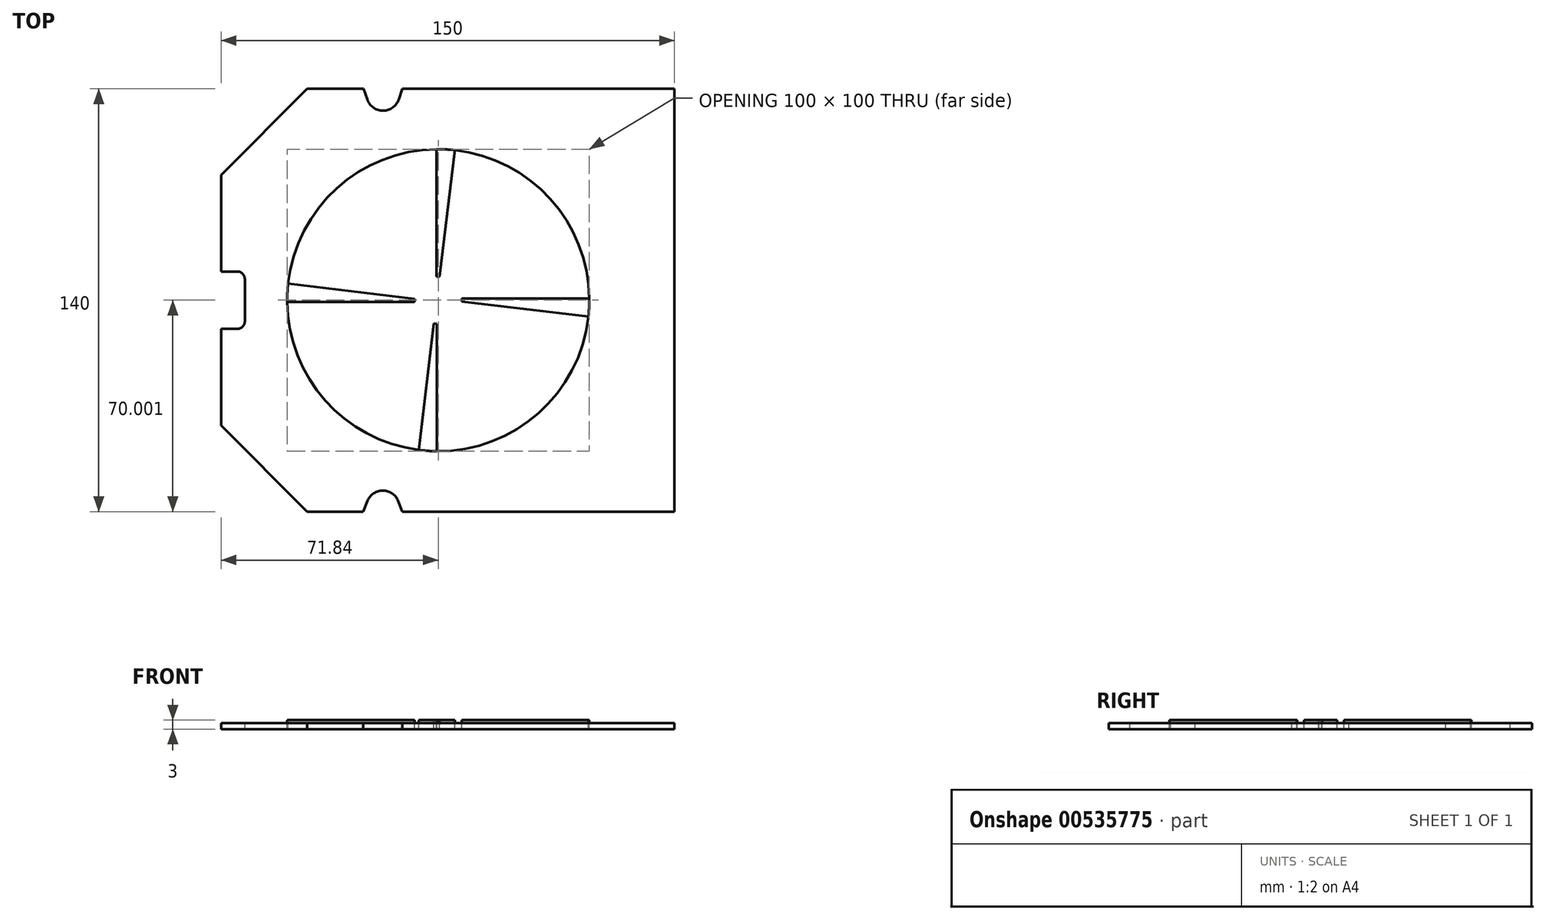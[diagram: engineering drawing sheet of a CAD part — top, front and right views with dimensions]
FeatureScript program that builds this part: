
annotation { "Feature Type Name" : "Feature", "Feature Type Description" : "" }
export const myFeature = defineFeature(function(context is Context, id is Id, definition is map)
    precondition{}
    {
        {
            var Q0;
            Q0=qCreatedBy(makeId("Top.planeOp"),FACE);
            var sketch = newSketch(context, id + "F0", { "sketchPlane" : qUnion([Q0])});
            skLineSegment(sketch, "E0.bottom", {"start": v(75, -70) * mm, "end": v(-75, -70) * mm});
            skLineSegment(sketch, "E0.top", {"start": v(75, 70) * mm, "end": v(-75, 70) * mm});
            skLineSegment(sketch, "E0.left", {"start": v(75, -70) * mm, "end": v(75, 70) * mm});
            skLineSegment(sketch, "E0.right", {"start": v(-75, -70) * mm, "end": v(-75, 70) * mm});
            skPoint(sketch, "E0.middle", {"position": v(0, 0) * mm});
            skSolve(sketch);
        }
        {
            var Q0;
            Q0=qSketchRegion(id+"F0",true);
            extrude(context, id + "F1", {"entities" : qUnion([Q0]), "depth" : 2 * mm, "offsetDistance" : 25 * mm});
        }
        {
            var Q0;
            Q0=makeQuery(id+"F1.opExtrude","CAP_FACE",FACE,{"disambiguationData":[OSD([sQuery(id+"F0.wireOp",EDGE,"E0.bottom"),sQuery(id+"F0.wireOp",EDGE,"E0.top"),sQuery(id+"F0.wireOp",EDGE,"E0.left"),sQuery(id+"F0.wireOp",EDGE,"E0.right")])],"isStart":false});
            var sketch = newSketch(context, id + "F2", { "sketchPlane" : qUnion([Q0])});
            skLineSegment(sketch, "E1", {"start": v(-75, 41.5) * mm, "end": v(-46.5, 70) * mm});
            skLineSegment(sketch, "E2", {"start": v(-75, -41.5) * mm, "end": v(-46.5, -70) * mm});
            skSolve(sketch);
        }
        {
            var Q0;
            Q0=qSketchRegion(id+"F2",true);
            var Q1;
            {var subQ0=sQuery(id+"F2.wireOp",EDGE,"E1");Q1=makeQuery(id+"F2.imprint","IMPRINT",FACE,{"disambiguationData":[TD([[makeQuery(id+"F2.imprint","IMPRINT",EDGE,{"derivedFrom":subQ0}),1.0]])]});}
            var Q2;
            {var subQ0=sQuery(id+"F2.wireOp",EDGE,"E2");Q2=makeQuery(id+"F2.imprint","IMPRINT",FACE,{"disambiguationData":[TD([[makeQuery(id+"F2.imprint","IMPRINT",EDGE,{"derivedFrom":subQ0}),-1.0]])]});}
            extrude(context, id + "F3", {"entities" : qUnion([Q0, Q1, Q2]), "operationType" : NewBodyOperationType.REMOVE, "endBound" : BoundingType.THROUGH_ALL, "oppositeDirection" : true, "depth" : 25 * mm, "offsetDistance" : 25 * mm});
        }
        {
            var Q0;
            Q0=makeQuery(id+"F1.opExtrude","CAP_FACE",FACE,{"disambiguationData":[OSD([sQuery(id+"F0.wireOp",EDGE,"E0.bottom"),sQuery(id+"F0.wireOp",EDGE,"E0.top"),sQuery(id+"F0.wireOp",EDGE,"E0.left"),sQuery(id+"F0.wireOp",EDGE,"E0.right")])],"isStart":false});
            var sketch = newSketch(context, id + "F4", { "sketchPlane" : qUnion([Q0])});
            skLineSegment(sketch, "E3", {"start": v(-75, 9.5) * mm, "end": v(-69.68, 9.5) * mm});
            skLineSegment(sketch, "E4", {"start": v(-67.18, 7) * mm, "end": v(-67.18, -7) * mm});
            skArc(sketch, "E5", {"start": v(-67.18, 7) * mm, "mid": v(-67.91, 8.77) * mm, "end": v(-69.68, 9.5) * mm});
            skLineSegment(sketch, "E6", {"start": v(-75, -9.5) * mm, "end": v(-69.68, -9.5) * mm});
            skArc(sketch, "E7", {"start": v(-69.68, -9.5) * mm, "mid": v(-67.91, -8.77) * mm, "end": v(-67.18, -7) * mm});
            skSolve(sketch);
        }
        {
            var Q0;
            Q0=qSketchRegion(id+"F4",true);
            var Q1;
            {var subQ1=sQuery(id+"F4.wireOp",EDGE,"E3");Q1=makeQuery(id+"F4.imprint","IMPRINT",FACE,{"disambiguationData":[TD([[makeQuery(id+"F4.imprint","IMPRINT",EDGE,{"derivedFrom":subQ1}),-1.0]])]});}
            extrude(context, id + "F5", {"entities" : qUnion([Q0, Q1]), "operationType" : NewBodyOperationType.REMOVE, "endBound" : BoundingType.THROUGH_ALL, "oppositeDirection" : true, "depth" : 25 * mm, "offsetDistance" : 25 * mm});
        }
        {
            var Q0;
            Q0=makeQuery(id+"F1.opExtrude","CAP_FACE",FACE,{"disambiguationData":[OSD([sQuery(id+"F0.wireOp",EDGE,"E0.bottom"),sQuery(id+"F0.wireOp",EDGE,"E0.top"),sQuery(id+"F0.wireOp",EDGE,"E0.left"),sQuery(id+"F0.wireOp",EDGE,"E0.right")])],"isStart":false});
            var sketch = newSketch(context, id + "F6", { "sketchPlane" : qUnion([Q0])});
            skArc(sketch, "E8", {"start": v(-26.63, 66.43) * mm, "mid": v(-21.44, 62.74) * mm, "end": v(-16.24, 66.43) * mm});
            skArc(sketch, "E9", {"start": v(-16.42, -66.5) * mm, "mid": v(-21.52, -63.06) * mm, "end": v(-26.61, -66.5) * mm});
            skLineSegment(sketch, "E10", {"start": v(-27.88, 70) * mm, "end": v(-26.63, 66.43) * mm});
            skLineSegment(sketch, "E11", {"start": v(-15, 70) * mm, "end": v(-16.24, 66.43) * mm});
            skLineSegment(sketch, "E12", {"start": v(-26.61, -66.5) * mm, "end": v(-28.03, -70) * mm});
            skLineSegment(sketch, "E13", {"start": v(-16.42, -66.5) * mm, "end": v(-15, -70) * mm});
            skSolve(sketch);
        }
        {
            var Q0;
            Q0=qSketchRegion(id+"F6",true);
            var Q1;
            Q1=makeQuery(id+"F6.imprint","IMPRINT",FACE,{"disambiguationData":[TD([[makeQuery(id+"F6.imprint","IMPRINT",EDGE,{"derivedFrom":sQuery(id+"F6.wireOp",EDGE,"E9")}),1.0]])]});
            var Q2;
            Q2=makeQuery(id+"F6.imprint","IMPRINT",FACE,{"disambiguationData":[TD([[makeQuery(id+"F6.imprint","IMPRINT",EDGE,{"derivedFrom":sQuery(id+"F6.wireOp",EDGE,"E8")}),1.0]])]});
            extrude(context, id + "F7", {"entities" : qUnion([Q0, Q1, Q2]), "operationType" : NewBodyOperationType.REMOVE, "endBound" : BoundingType.THROUGH_ALL, "oppositeDirection" : true, "depth" : 25 * mm, "offsetDistance" : 25 * mm});
        }
        {
            var Q0;
            Q0=makeQuery(id+"F1.opExtrude","CAP_FACE",FACE,{"disambiguationData":[OSD([sQuery(id+"F0.wireOp",EDGE,"E0.bottom"),sQuery(id+"F0.wireOp",EDGE,"E0.top"),sQuery(id+"F0.wireOp",EDGE,"E0.left"),sQuery(id+"F0.wireOp",EDGE,"E0.right")])],"isStart":false});
            var sketch = newSketch(context, id + "F8", { "sketchPlane" : qUnion([Q0])});
            skCircle(sketch, "E14", {"center": v(-3.16, 0) * mm, "radius": 50 * mm});
            skPoint(sketch, "E14.first.point", {"position": v(-36.36, 37.39) * mm});
            skPoint(sketch, "E14.second.point", {"position": v(32.35, -35.2) * mm});
            skPoint(sketch, "E14.third.point", {"position": v(42.82, 19.64) * mm});
            skSolve(sketch);
        }
        {
            var Q0;
            Q0=qSketchRegion(id+"F8",true);
            extrude(context, id + "F9", {"entities" : qUnion([Q0]), "operationType" : NewBodyOperationType.ADD, "depth" : 1 * mm, "offsetDistance" : 25 * mm});
        }
        {
            var Q0;
            Q0=makeQuery(id+"F9.opExtrude","CAP_FACE",FACE,{"disambiguationData":[OSD([sQuery(id+"F8.wireOp",EDGE,"E14")])],"isStart":false});
            var sketch = newSketch(context, id + "F10", { "sketchPlane" : qUnion([Q0])});
            skLineSegment(sketch, "E15", {"start": v(-3.7, 50) * mm, "end": v(2.3, 49.7) * mm});
            skLineSegment(sketch, "E16", {"start": v(-2.69, 7.84) * mm, "end": v(-3.69, 7.84) * mm});
            skLineSegment(sketch, "E17", {"start": v(-3.69, 7.84) * mm, "end": v(-3.7, 50) * mm});
            skLineSegment(sketch, "E18", {"start": v(2.3, 49.7) * mm, "end": v(-2.69, 7.84) * mm});
            skLineSegment(sketch, "E19", {"start": v(46.84, 0.53) * mm, "end": v(4.68, 0.53) * mm});
            skLineSegment(sketch, "E20", {"start": v(4.68, 0.53) * mm, "end": v(4.68, -0.47) * mm});
            skLineSegment(sketch, "E21", {"start": v(4.68, -0.47) * mm, "end": v(46.54, -5.46) * mm});
            skLineSegment(sketch, "E22", {"start": v(46.54, -5.46) * mm, "end": v(46.84, 0.53) * mm});
            skLineSegment(sketch, "E23", {"start": v(-3.62, -50) * mm, "end": v(-9.6, -49.58) * mm});
            skLineSegment(sketch, "E24", {"start": v(-9.6, -49.58) * mm, "end": v(-4.61, -7.72) * mm});
            skLineSegment(sketch, "E25", {"start": v(-4.61, -7.72) * mm, "end": v(-3.62, -7.84) * mm});
            skLineSegment(sketch, "E26", {"start": v(-3.62, -7.84) * mm, "end": v(-3.62, -50) * mm});
            skLineSegment(sketch, "E27", {"start": v(-52.86, 5.47) * mm, "end": v(-11, 0.47) * mm});
            skLineSegment(sketch, "E28", {"start": v(-11, 0.47) * mm, "end": v(-11, -0.53) * mm});
            skLineSegment(sketch, "E29", {"start": v(-11, -0.53) * mm, "end": v(-53.16, -0.53) * mm});
            skLineSegment(sketch, "E30", {"start": v(-53.16, -0.53) * mm, "end": v(-52.86, 5.47) * mm});
            skSolve(sketch);
        }
        {
            var Q0;
            Q0=makeQuery(id+"F10.imprint","IMPRINT",FACE,{"disambiguationData":[TD([[makeQuery(id+"F10.imprint","IMPRINT",EDGE,{"derivedFrom":sQuery(id+"F10.wireOp",EDGE,"E16")}),1.0]])]});
            extrude(context, id + "F11", {"entities" : qUnion([Q0]), "operationType" : NewBodyOperationType.REMOVE, "oppositeDirection" : true, "depth" : 25 * mm, "offsetDistance" : 25 * mm});
        }
    });
